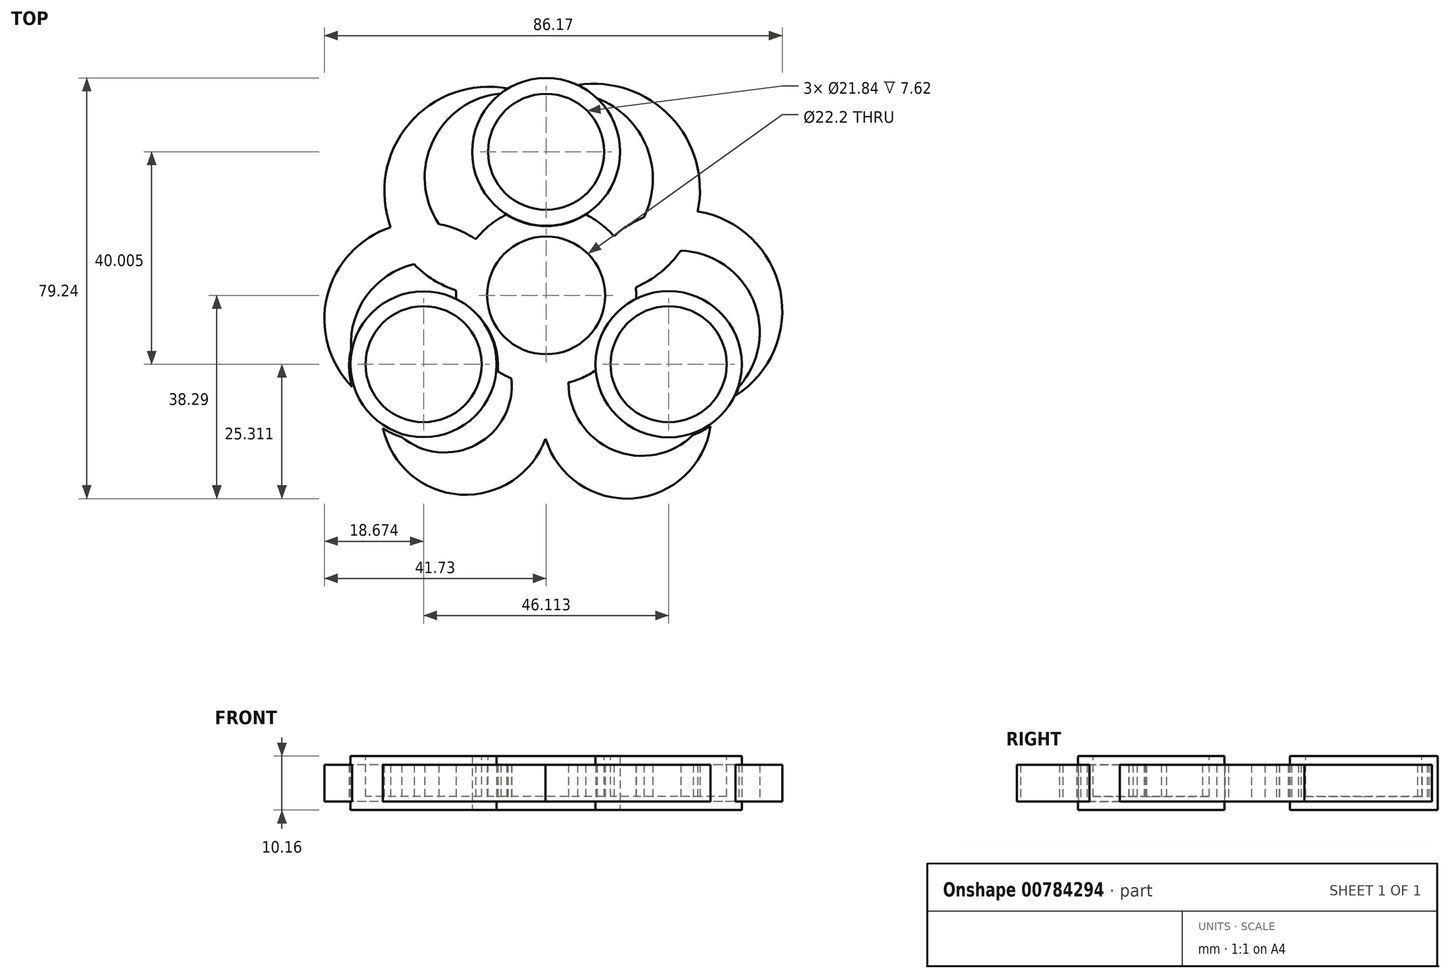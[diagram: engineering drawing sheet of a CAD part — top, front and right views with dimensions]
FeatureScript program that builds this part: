
annotation { "Feature Type Name" : "Feature", "Feature Type Description" : "" }
export const myFeature = defineFeature(function(context is Context, id is Id, definition is map)
    precondition{}
    {
        {
            var Q0;
            Q0=qCreatedBy(makeId("Top.planeOp"),FACE);
            var sketch = newSketch(context, id + "F0", { "sketchPlane" : qUnion([Q0])});
            skCircle(sketch, "E0", {"center": v(0, 0) * mm, "radius": 11.1 * mm});
            skCircle(sketch, "E1", {"center": v(0, 26.63) * mm, "radius": 11.1 * mm});
            skCircle(sketch, "E2.1.0", {"center": v(-23.07, -13.32) * mm, "radius": 11.1 * mm});
            skCircle(sketch, "E2.2.0", {"center": v(23.07, -13.32) * mm, "radius": 11.1 * mm});
            skArc(sketch, "E3", {"start": v(-7.43, 15.23) * mm, "mid": v(-10.6, 13.22) * mm, "end": v(-13.27, 10.55) * mm});
            skArc(sketch, "E4", {"start": v(-10.62, 18.13) * mm, "mid": v(-14.05, 15.62) * mm, "end": v(-16.9, 12.48) * mm});
            skArc(sketch, "E5.trimOffspring", {"start": v(21.01, 0.3) * mm, "mid": v(20.92, 2) * mm, "end": v(20.69, 3.7) * mm});
            skArc(sketch, "E6.trimOffspring", {"start": v(16.92, -1) * mm, "mid": v(16.95, 0.26) * mm, "end": v(16.88, 1.52) * mm});
            skArc(sketch, "E7.trimOffspring", {"start": v(-10.05, -18.45) * mm, "mid": v(-8.45, -19.24) * mm, "end": v(-6.8, -19.88) * mm});
            skArc(sketch, "E8.trimOffspring", {"start": v(-9.1, -14.3) * mm, "mid": v(-7.84, -15.03) * mm, "end": v(-6.51, -15.65) * mm});
            skArc(sketch, "E9", {"start": v(-7.33, 38.1) * mm, "mid": v(-21.06, 29.56) * mm, "end": v(-20.19, 13.42) * mm});
            skArc(sketch, "E10", {"start": v(18.4, 14.68) * mm, "mid": v(18.64, 28.61) * mm, "end": v(8.02, 37.63) * mm});
            skArc(sketch, "E11", {"start": v(-6.2, 38.75) * mm, "mid": v(-25.48, 32.68) * mm, "end": v(-29.24, 12.82) * mm});
            skArc(sketch, "E12", {"start": v(16.88, 1.52) * mm, "mid": v(21.59, 4.38) * mm, "end": v(25.33, 8.42) * mm});
            skArc(sketch, "E13", {"start": v(-13.27, 10.55) * mm, "mid": v(-16.58, 12.35) * mm, "end": v(-20.19, 13.42) * mm});
            skArc(sketch, "E14", {"start": v(36.26, -17.24) * mm, "mid": v(38.97, -0.93) * mm, "end": v(25.33, 8.42) * mm});
            skArc(sketch, "E15", {"start": v(35.65, -18.9) * mm, "mid": v(44.05, 0.91) * mm, "end": v(28.52, 15.81) * mm});
            skArc(sketch, "E16.trimOffspring", {"start": v(18.4, 14.68) * mm, "mid": v(15.42, 13.17) * mm, "end": v(12.76, 11.15) * mm});
            skArc(sketch, "E17.trimOffspring", {"start": v(28.52, 15.81) * mm, "mid": v(23.02, 34.06) * mm, "end": v(4.72, 39.4) * mm});
            skArc(sketch, "E18.trimOffspring", {"start": v(12.76, 11.15) * mm, "mid": v(10.3, 13.46) * mm, "end": v(7.43, 15.23) * mm});
            skArc(sketch, "E19.trimOffspring", {"start": v(16.06, 13.55) * mm, "mid": v(13.54, 16.07) * mm, "end": v(10.62, 18.13) * mm});
            skArc(sketch, "E20.trimOffspring", {"start": v(-24.84, 5.85) * mm, "mid": v(-33.7, 0.04) * mm, "end": v(-36.7, -10.13) * mm});
            skArc(sketch, "E21.trimOffspring", {"start": v(-16.92, 0.91) * mm, "mid": v(-16.95, 0.09) * mm, "end": v(-16.93, -0.74) * mm});
            skArc(sketch, "E22.trimOffspring", {"start": v(-20.84, 2.7) * mm, "mid": v(-20.95, 1.61) * mm, "end": v(-21, 0.52) * mm});
            skArc(sketch, "E23.trimOffspring", {"start": v(-29.24, 12.82) * mm, "mid": v(-41.22, -0.18) * mm, "end": v(-36.5, -17.2) * mm});
            skArc(sketch, "E24.trimOffspring", {"start": v(-24.84, 5.85) * mm, "mid": v(-21.18, 2.9) * mm, "end": v(-16.92, 0.91) * mm});
            skPoint(sketch, "E25.orphan", {"position": v(-9.01, 6.48) * mm});
            skPoint(sketch, "E26.trimOffspring.end.orphan", {"position": v(-9.01, 0) * mm});
            skPoint(sketch, "E27.orphan", {"position": v(9.01, 6.48) * mm});
            skPoint(sketch, "E28.orphan", {"position": v(11.1, 0) * mm});
            skArc(sketch, "E29", {"start": v(4.2, -16.42) * mm, "mid": v(12.68, -29.16) * mm, "end": v(27.71, -26.27) * mm});
            skArc(sketch, "E30", {"start": v(-27.14, -26.7) * mm, "mid": v(-13.12, -28.1) * mm, "end": v(-6.51, -15.65) * mm});
            skArc(sketch, "E31", {"start": v(-30.7, -25.04) * mm, "mid": v(-16.14, -37.53) * mm, "end": v(-0.1, -27) * mm});
            skArc(sketch, "E32.trimOffspring", {"start": v(4.8, -20.46) * mm, "mid": v(7.6, -19.59) * mm, "end": v(10.25, -18.34) * mm});
            skArc(sketch, "E33.trimOffspring", {"start": v(4.2, -16.42) * mm, "mid": v(6.86, -15.5) * mm, "end": v(9.33, -14.15) * mm});
            skArc(sketch, "E34.trimOffspring", {"start": v(-0.1, -27) * mm, "mid": v(16.39, -38.24) * mm, "end": v(30.96, -24.6) * mm});
            skArc(sketch, "E35", {"start": v(16.92, -1) * mm, "mid": v(11.15, -6.44) * mm, "end": v(9.33, -14.15) * mm});
            skArc(sketch, "E36", {"start": v(-21, 0.52) * mm, "mid": v(-35.18, -20.31) * mm, "end": v(-10.05, -18.45) * mm});
            skArc(sketch, "E37", {"start": v(10.62, 18.13) * mm, "mid": v(0, 40.24) * mm, "end": v(-10.62, 18.13) * mm});
            skPoint(sketch, "E38.orphan", {"position": v(31.07, -21.01) * mm});
            skPoint(sketch, "E39.orphan", {"position": v(12.06, -11.91) * mm});
            skPoint(sketch, "E40.orphan", {"position": v(-31.07, -21.01) * mm});
            skArc(sketch, "E41.trimOffspring", {"start": v(-7.43, 15.23) * mm, "mid": v(0, 13.03) * mm, "end": v(7.43, 15.23) * mm});
            skArc(sketch, "E42.trimOffspring", {"start": v(10.25, -18.34) * mm, "mid": v(34.99, -20.2) * mm, "end": v(21.01, 0.3) * mm});
            skArc(sketch, "E43.trimOffspring", {"start": v(-9.1, -14.3) * mm, "mid": v(-10.95, -6.32) * mm, "end": v(-16.93, -0.74) * mm});
            skPoint(sketch, "E44.orphan", {"position": v(0, 37.73) * mm});
            skSolve(sketch);
        }
        {
            var Q0;
            Q0=qCreatedBy(makeId("Top.planeOp"),FACE);
            var sketch = newSketch(context, id + "F1", { "sketchPlane" : qUnion([Q0])});
            skCircle(sketch, "E45", {"center": v(23.06, -12.98) * mm, "radius": 13.77 * mm});
            skSolve(sketch);
        }
        {
            var Q0;
            Q0=qCreatedBy(makeId("Top.planeOp"),FACE);
            var sketch = newSketch(context, id + "F2", { "sketchPlane" : qUnion([Q0])});
            skCircle(sketch, "E46", {"center": v(-23.06, -12.98) * mm, "radius": 13.75 * mm});
            skCircle(sketch, "E47", {"center": v(0, 27.03) * mm, "radius": 13.93 * mm});
            skSolve(sketch);
        }
        {
            var Q0;
            Q0=makeQuery(id+"F0.imprint","IMPRINT",FACE,{"disambiguationData":[TD([[makeQuery(id+"F0.imprint","IMPRINT",EDGE,{"derivedFrom":sQuery(id+"F0.wireOp",EDGE,"E0")}),-1.0]])]});
            extrude(context, id + "F3", {"entities" : qUnion([Q0]), "endBound" : BoundingType.SYMMETRIC, "depth" : 6.93 * mm, "offsetDistance" : 25.4 * mm});
        }
        {
            var Q0;
            Q0=makeQuery(id+"F2.imprint","IMPRINT",FACE,{"disambiguationData":[TD([[makeQuery(id+"F2.imprint","IMPRINT",EDGE,{"derivedFrom":sQuery(id+"F2.wireOp",EDGE,"E47")}),1.0]])]});
            var Q1;
            Q1=makeQuery(id+"F2.imprint","IMPRINT",FACE,{"disambiguationData":[TD([[makeQuery(id+"F2.imprint","IMPRINT",EDGE,{"derivedFrom":sQuery(id+"F2.wireOp",EDGE,"E46")}),1.0]])]});
            var Q2;
            Q2=makeQuery(id+"F1.imprint","IMPRINT",FACE,{"disambiguationData":[TD([[makeQuery(id+"F1.imprint","IMPRINT",EDGE,{"derivedFrom":sQuery(id+"F1.wireOp",EDGE,"E45")}),1.0]])]});
            extrude(context, id + "F4", {"entities" : qUnion([Q0, Q1, Q2]), "operationType" : NewBodyOperationType.ADD, "endBound" : BoundingType.SYMMETRIC, "depth" : 10.16 * mm, "offsetDistance" : 25.4 * mm});
        }
        {
            var Q0;
            Q0=makeQuery(id+"F4.opExtrude","CAP_FACE",FACE,{"disambiguationData":[OSD([sQuery(id+"F2.wireOp",EDGE,"E46")])],"isStart":false});
            var sketch = newSketch(context, id + "F5", { "sketchPlane" : qUnion([Q0])});
            skCircle(sketch, "E48", {"center": v(-23.06, -12.98) * mm, "radius": 10.92 * mm});
            skCircle(sketch, "E49", {"center": v(0, 27.03) * mm, "radius": 10.92 * mm});
            skCircle(sketch, "E50", {"center": v(23.06, -12.98) * mm, "radius": 10.92 * mm});
            skSolve(sketch);
        }
        {
            var Q0;
            Q0=makeQuery(id+"F5.imprint","IMPRINT",FACE,{"disambiguationData":[TD([[makeQuery(id+"F5.imprint","IMPRINT",EDGE,{"derivedFrom":sQuery(id+"F5.wireOp",EDGE,"E49")}),1.0]])]});
            var Q1;
            Q1=makeQuery(id+"F5.imprint","IMPRINT",FACE,{"disambiguationData":[TD([[makeQuery(id+"F5.imprint","IMPRINT",EDGE,{"derivedFrom":sQuery(id+"F5.wireOp",EDGE,"E48")}),1.0]])]});
            var Q2;
            Q2=makeQuery(id+"F5.imprint","IMPRINT",FACE,{"disambiguationData":[TD([[makeQuery(id+"F5.imprint","IMPRINT",EDGE,{"derivedFrom":sQuery(id+"F5.wireOp",EDGE,"E50")}),1.0]])]});
            extrude(context, id + "F6", {"entities" : qUnion([Q0, Q1, Q2]), "operationType" : NewBodyOperationType.REMOVE, "oppositeDirection" : true, "depth" : 7.62 * mm, "offsetDistance" : 25.4 * mm});
        }
    });
